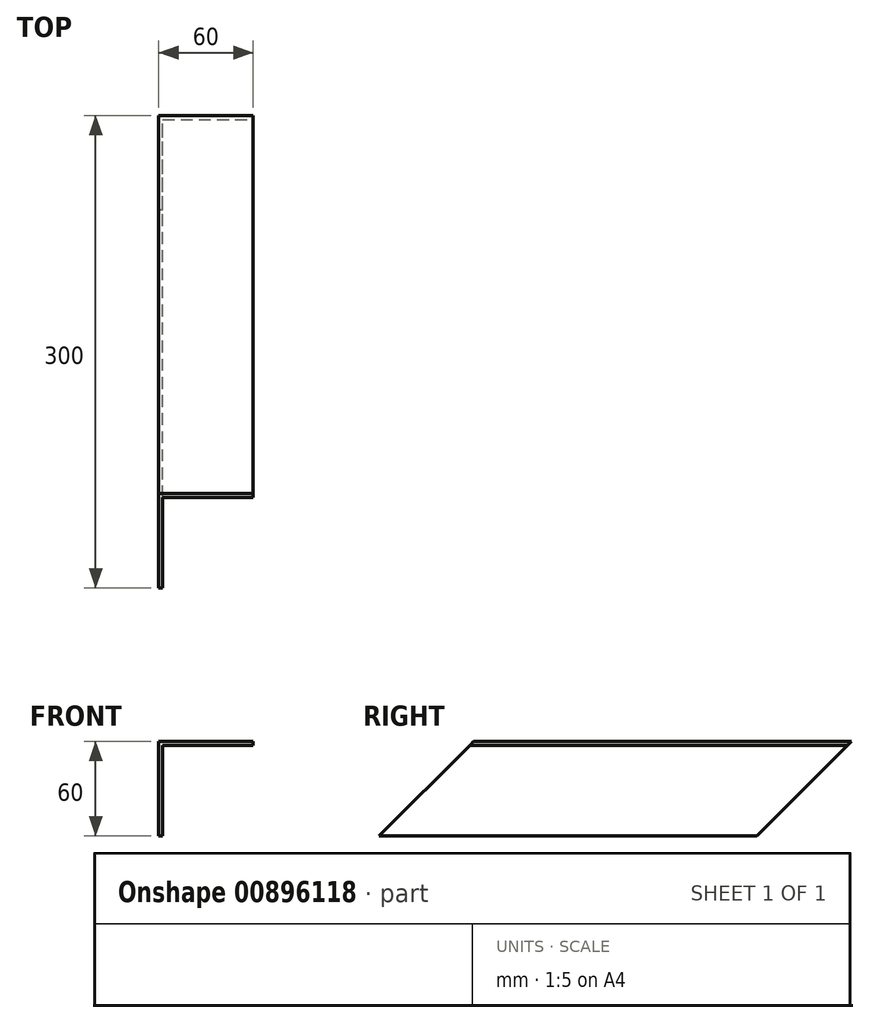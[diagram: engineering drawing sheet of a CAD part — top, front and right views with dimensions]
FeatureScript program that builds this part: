
annotation { "Feature Type Name" : "Feature", "Feature Type Description" : "" }
export const myFeature = defineFeature(function(context is Context, id is Id, definition is map)
    precondition{}
    {
        {
            var Q0;
            Q0=qCreatedBy(makeId("Front.planeOp"),FACE);
            var sketch = newSketch(context, id + "F0", { "sketchPlane" : qUnion([Q0])});
            skLineSegment(sketch, "E0", {"start": v(0, 0) * mm, "end": v(60, 0) * mm});
            skLineSegment(sketch, "E1", {"start": v(60, 0) * mm, "end": v(60, -2.5) * mm});
            skLineSegment(sketch, "E2", {"start": v(60, -2.5) * mm, "end": v(2.5, -2.5) * mm});
            skLineSegment(sketch, "E3", {"start": v(2.5, -2.5) * mm, "end": v(2.5, -60) * mm});
            skLineSegment(sketch, "E4", {"start": v(2.5, -60) * mm, "end": v(0, -60) * mm});
            skLineSegment(sketch, "E5", {"start": v(0, -60) * mm, "end": v(0, 0) * mm});
            skSolve(sketch);
        }
        {
            var Q0;
            Q0=qSketchRegion(id+"F0",true);
            extrude(context, id + "F1", {"entities" : qUnion([Q0]), "depth" : 300 * mm, "offsetDistance" : 25 * mm});
        }
        {
            var Q0;
            Q0=makeQuery(id+"F1.opExtrude","SWEPT_FACE",FACE,{"disambiguationData":[OSD([sQuery(id+"F0.wireOp",EDGE,"E5")])]});
            var sketch = newSketch(context, id + "F2", { "sketchPlane" : qUnion([Q0])});
            skLineSegment(sketch, "E6", {"start": v(0, -60) * mm, "end": v(0, 0) * mm});
            skLineSegment(sketch, "E7", {"start": v(0, 0) * mm, "end": v(60, -60) * mm});
            skLineSegment(sketch, "E8", {"start": v(60, -60) * mm, "end": v(0, -60) * mm});
            skSolve(sketch);
        }
        {
            var Q0;
            Q0=makeQuery(id+"F2.imprint","IMPRINT",FACE,{"disambiguationData":[TD([[makeQuery(id+"F2.imprint","IMPRINT",EDGE,{"derivedFrom":sQuery(id+"F2.wireOp",EDGE,"E6")}),-1.0]])]});
            extrude(context, id + "F3", {"entities" : qUnion([Q0]), "operationType" : NewBodyOperationType.REMOVE, "endBound" : BoundingType.THROUGH_ALL, "oppositeDirection" : true, "depth" : 25 * mm, "offsetDistance" : 25 * mm});
        }
        {
            var Q0;
            Q0=makeQuery(id+"F1.opExtrude","SWEPT_FACE",FACE,{"disambiguationData":[OSD([sQuery(id+"F0.wireOp",EDGE,"E5")])]});
            var sketch = newSketch(context, id + "F4", { "sketchPlane" : qUnion([Q0])});
            skLineSegment(sketch, "E9", {"start": v(300, -60) * mm, "end": v(240, 0) * mm});
            skLineSegment(sketch, "E10", {"start": v(240, 0) * mm, "end": v(300, 0) * mm});
            skLineSegment(sketch, "E11", {"start": v(300, 0) * mm, "end": v(300, -60) * mm});
            skSolve(sketch);
        }
        {
            var Q0;
            Q0=makeQuery(id+"F4.imprint","IMPRINT",FACE,{"disambiguationData":[TD([[makeQuery(id+"F4.imprint","IMPRINT",EDGE,{"derivedFrom":sQuery(id+"F4.wireOp",EDGE,"E9")}),-1.0]])]});
            extrude(context, id + "F5", {"entities" : qUnion([Q0]), "operationType" : NewBodyOperationType.REMOVE, "endBound" : BoundingType.THROUGH_ALL, "oppositeDirection" : true, "depth" : 25 * mm, "offsetDistance" : 25 * mm});
        }
    });
